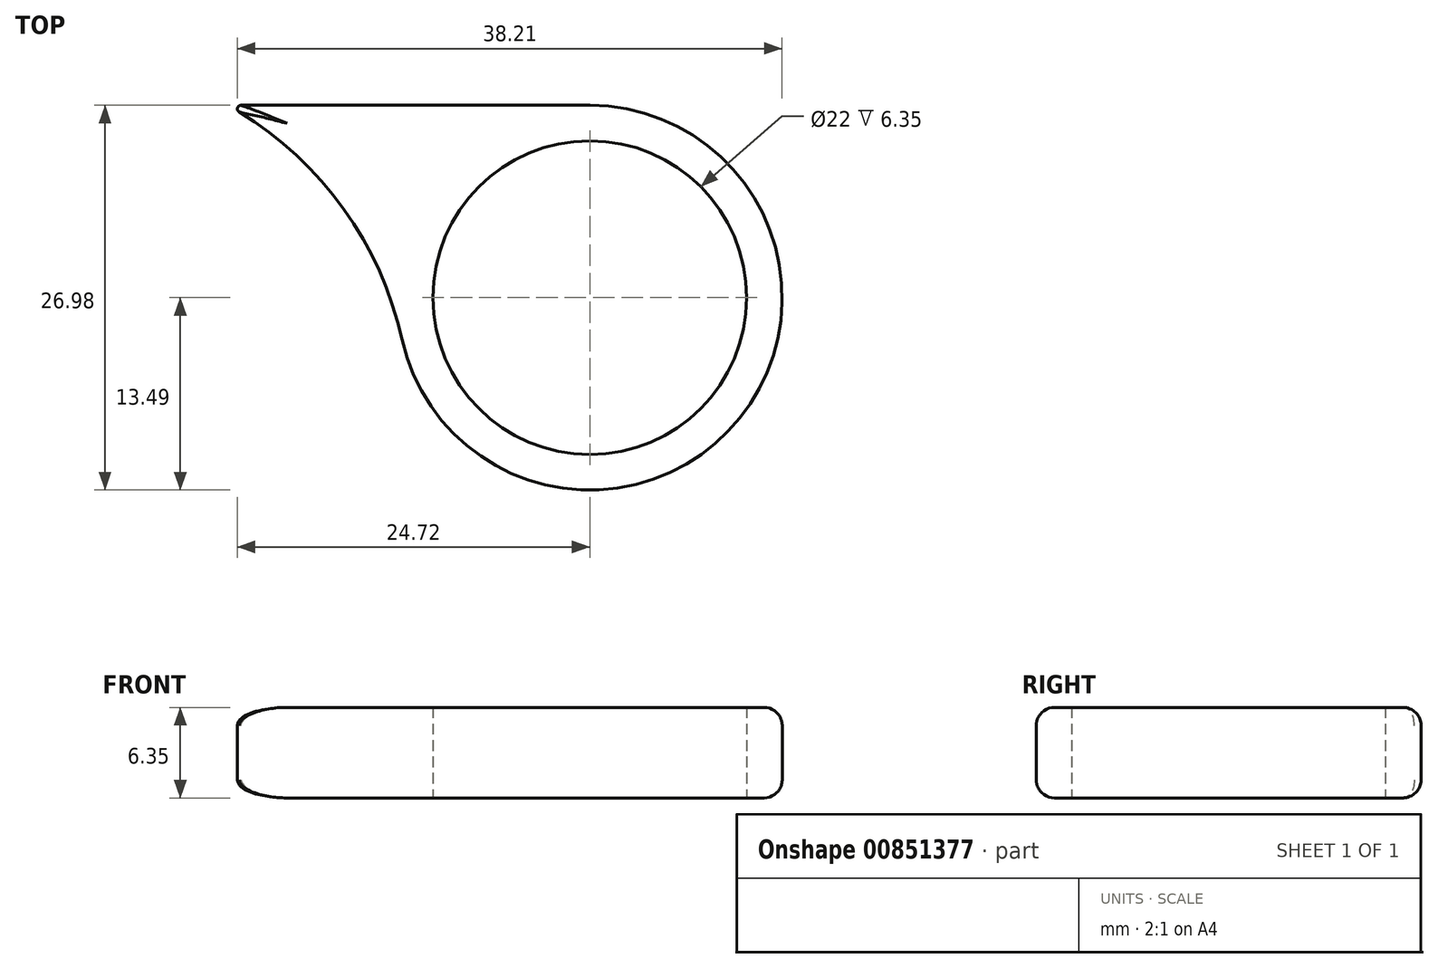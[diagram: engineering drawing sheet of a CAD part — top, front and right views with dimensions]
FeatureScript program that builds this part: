
annotation { "Feature Type Name" : "Feature", "Feature Type Description" : "" }
export const myFeature = defineFeature(function(context is Context, id is Id, definition is map)
    precondition{}
    {
        {
            var Q0;
            Q0=qCreatedBy(makeId("Top.planeOp"),FACE);
            var sketch = newSketch(context, id + "F0", { "sketchPlane" : qUnion([Q0])});
            skCircle(sketch, "E0", {"center": v(0, 0) * mm, "radius": 11 * mm});
            skCircle(sketch, "E1", {"center": v(0, 0) * mm, "radius": 13.5 * mm});
            skLineSegment(sketch, "E2", {"start": v(0, 13.5) * mm, "end": v(-25.4, 13.5) * mm});
            skArc(sketch, "E3", {"start": v(-13.17, -2.93) * mm, "mid": v(-17.53, 6.59) * mm, "end": v(-25.4, 13.5) * mm});
            skSolve(sketch);
        }
        {
            var Q0;
            Q0=makeQuery(id+"F0.imprint","IMPRINT",FACE,{"disambiguationData":[TD([[makeQuery(id+"F0.imprint","IMPRINT",EDGE,{"derivedFrom":sQuery(id+"F0.wireOp",EDGE,"E0")}),-1.0]])]});
            extrude(context, id + "F1", {"entities" : qUnion([Q0]), "depth" : 6.35 * mm, "offsetDistance" : 25.4 * mm});
        }
        {
            var Q0;
            Q0 = qSketchRegion(id + "F0", true);
            extrude(context, id + "F2", {"entities" : qUnion([Q0]), "operationType" : NewBodyOperationType.ADD, "depth" : 6.35 * mm, "offsetDistance" : 25.4 * mm});
        }
        {
            var Q0;
            Q0=makeQuery(id+"F2.opExtrude","SWEPT_EDGE",EDGE,{"disambiguationData":[OSD([sQuery(id+"F0.wireOp",EDGE,"E2"),sQuery(id+"F0.wireOp",EDGE,"E3")])]});
            fillet(context, id + "F3", {"entities" : qUnion([Q0]), "radius" : 0.25 * mm, "tangentPropagation" : true, "allowEdgeOverflow" : false});
        }
        {
            var Q0;
            Q0=makeQuery(id+"F2.opExtrude","CAP_EDGE",EDGE,{"disambiguationData":[OSD([sQuery(id+"F0.wireOp",EDGE,"E2")])],"isStart":false});
            var Q1;
            Q1=makeQuery(id+"F2.opExtrude","CAP_EDGE",EDGE,{"disambiguationData":[OSD([sQuery(id+"F0.wireOp",EDGE,"E3")])],"isStart":false});
            fillet(context, id + "F4", {"entities" : qUnion([Q0, Q1]), "radius" : 1.27 * mm, "tangentPropagation" : true, "allowEdgeOverflow" : false});
        }
        {
            var Q0;
            Q0=makeQuery(id+"F1.opExtrude","CAP_EDGE",EDGE,{"disambiguationData":[OSD([sQuery(id+"F0.wireOp",EDGE,"E1")])],"isStart":true});
            var Q1;
            Q1=makeQuery(id+"F2.opExtrude","CAP_EDGE",EDGE,{"disambiguationData":[OSD([sQuery(id+"F0.wireOp",EDGE,"E3")])],"isStart":true});
            var Q2;
            Q2=makeQuery(id+"F2.opExtrude","CAP_EDGE",EDGE,{"disambiguationData":[OSD([sQuery(id+"F0.wireOp",EDGE,"E2")])],"isStart":true});
            fillet(context, id + "F5", {"entities" : qUnion([Q0, Q1, Q2]), "radius" : 1.27 * mm, "tangentPropagation" : true, "allowEdgeOverflow" : false});
        }
    });
